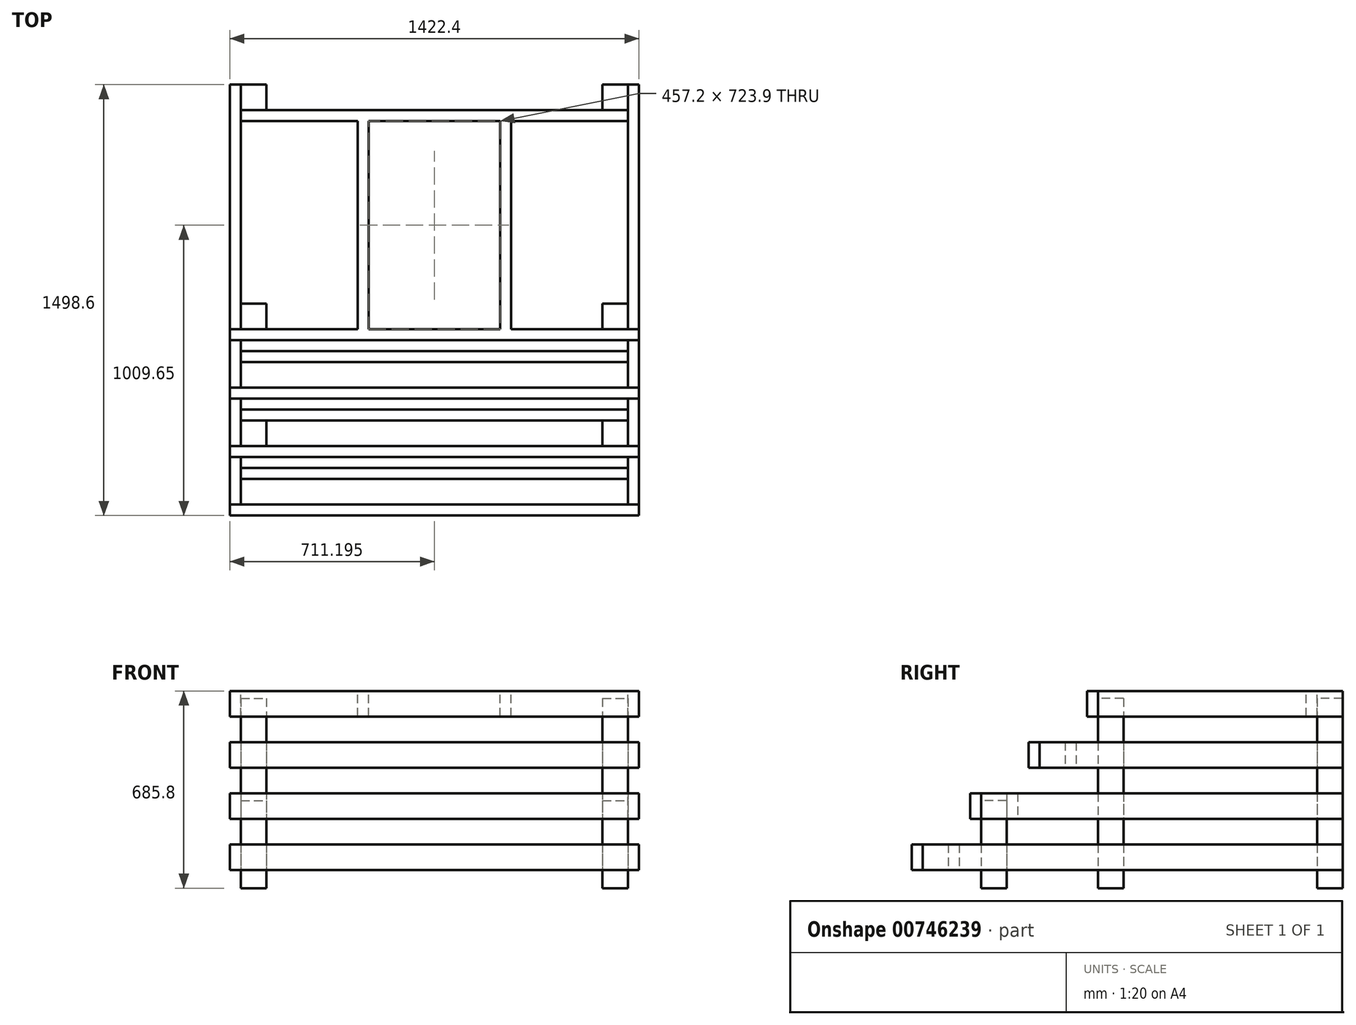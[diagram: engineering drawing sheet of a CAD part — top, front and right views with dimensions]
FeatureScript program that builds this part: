
annotation { "Feature Type Name" : "Feature", "Feature Type Description" : "" }
export const myFeature = defineFeature(function(context is Context, id is Id, definition is map)
    precondition{}
    {
        {
            var Q0;
            Q0=qCreatedBy(makeId("Top.planeOp"),FACE);
            var sketch = newSketch(context, id + "F0", { "sketchPlane" : qUnion([Q0])});
            skLineSegment(sketch, "E0.bottom", {"start": v(-670.31, 449.54) * mm, "end": v(-581.41, 449.54) * mm});
            skLineSegment(sketch, "E0.top", {"start": v(-670.31, 360.64) * mm, "end": v(-581.41, 360.64) * mm});
            skLineSegment(sketch, "E0.left", {"start": v(-670.31, 449.54) * mm, "end": v(-670.31, 360.64) * mm});
            skLineSegment(sketch, "E0.right", {"start": v(-581.41, 449.54) * mm, "end": v(-581.41, 360.64) * mm});
            skLineSegment(sketch, "E1.bottom", {"start": v(586.99, 449.54) * mm, "end": v(675.89, 449.54) * mm});
            skLineSegment(sketch, "E1.top", {"start": v(586.99, 360.64) * mm, "end": v(675.89, 360.64) * mm});
            skLineSegment(sketch, "E1.left", {"start": v(586.99, 449.54) * mm, "end": v(586.99, 360.64) * mm});
            skLineSegment(sketch, "E1.right", {"start": v(675.89, 449.54) * mm, "end": v(675.89, 360.64) * mm});
            skLineSegment(sketch, "E2.bottom", {"start": v(-670.31, -312.46) * mm, "end": v(-581.41, -312.46) * mm});
            skLineSegment(sketch, "E2.top", {"start": v(-670.31, -401.36) * mm, "end": v(-581.41, -401.36) * mm});
            skLineSegment(sketch, "E2.left", {"start": v(-670.31, -312.46) * mm, "end": v(-670.31, -401.36) * mm});
            skLineSegment(sketch, "E2.right", {"start": v(-581.41, -312.46) * mm, "end": v(-581.41, -401.36) * mm});
            skLineSegment(sketch, "E3.bottom", {"start": v(586.99, -312.46) * mm, "end": v(675.89, -312.46) * mm});
            skLineSegment(sketch, "E3.top", {"start": v(586.99, -401.36) * mm, "end": v(675.89, -401.36) * mm});
            skLineSegment(sketch, "E3.left", {"start": v(586.99, -312.46) * mm, "end": v(586.99, -401.36) * mm});
            skLineSegment(sketch, "E3.right", {"start": v(675.89, -312.46) * mm, "end": v(675.89, -401.36) * mm});
            skLineSegment(sketch, "E4.bottom", {"start": v(-670.31, -718.86) * mm, "end": v(-581.41, -718.86) * mm});
            skLineSegment(sketch, "E4.top", {"start": v(-670.31, -807.76) * mm, "end": v(-581.41, -807.76) * mm});
            skLineSegment(sketch, "E4.left", {"start": v(-670.31, -718.86) * mm, "end": v(-670.31, -807.76) * mm});
            skLineSegment(sketch, "E4.right", {"start": v(-581.41, -718.86) * mm, "end": v(-581.41, -807.76) * mm});
            skLineSegment(sketch, "E5.bottom", {"start": v(586.99, -718.86) * mm, "end": v(675.89, -718.86) * mm});
            skLineSegment(sketch, "E5.top", {"start": v(586.99, -807.76) * mm, "end": v(675.89, -807.76) * mm});
            skLineSegment(sketch, "E5.left", {"start": v(586.99, -718.86) * mm, "end": v(586.99, -807.76) * mm});
            skLineSegment(sketch, "E5.right", {"start": v(675.89, -718.86) * mm, "end": v(675.89, -807.76) * mm});
            skSolve(sketch);
        }
        {
            var Q0;
            Q0 = qSketchRegion(id + "F0", true);
            extrude(context, id + "F1", {"entities" : qUnion([Q0]), "depth" : 660.4 * mm, "offsetDistance" : 25.4 * mm});
        }
        {
            var Q0;
            Q0=qCreatedBy(makeId("Right.planeOp"),FACE);
            var sketch = newSketch(context, id + "F2", { "sketchPlane" : qUnion([Q0])});
            skLineSegment(sketch, "E6.bottom", {"start": v(-597.65, 708) * mm, "end": v(-967.88, 708) * mm});
            skLineSegment(sketch, "E6.top", {"start": v(-597.65, 304.8) * mm, "end": v(-967.88, 304.8) * mm});
            skLineSegment(sketch, "E6.left", {"start": v(-597.65, 708) * mm, "end": v(-597.65, 304.8) * mm});
            skLineSegment(sketch, "E6.right", {"start": v(-967.88, 708) * mm, "end": v(-967.88, 304.8) * mm});
            skSolve(sketch);
        }
        {
            var Q0;
            Q0 = qSketchRegion(id + "F2", true);
            extrude(context, id + "F3", {"entities" : qUnion([Q0]), "operationType" : NewBodyOperationType.REMOVE, "oppositeDirection" : true, "depth" : 1183.64 * mm, "offsetDistance" : 25.4 * mm, "hasSecondDirection" : true, "secondDirectionOppositeDirection" : false, "secondDirectionDepth" : 1132.84 * mm});
        }
        {
            var Q0;
            Q0=makeQuery(id+"F1.opExtrude","SWEPT_FACE",FACE,{"disambiguationData":[OSD([sQuery(id+"F0.wireOp",EDGE,"E4.top")])]});
            var sketch = newSketch(context, id + "F4", { "sketchPlane" : qUnion([Q0])});
            skLineSegment(sketch, "E7.bottom", {"start": v(-670.31, 596.9) * mm, "end": v(-708.41, 596.9) * mm});
            skLineSegment(sketch, "E7.top", {"start": v(-670.31, 685.8) * mm, "end": v(-708.41, 685.8) * mm});
            skLineSegment(sketch, "E7.left", {"start": v(-670.31, 596.9) * mm, "end": v(-670.31, 685.8) * mm});
            skLineSegment(sketch, "E7.right", {"start": v(-708.41, 596.9) * mm, "end": v(-708.41, 685.8) * mm});
            skPoint(sketch, "E8.firstSnap0", {"position": v(-689.36, 596.9) * mm});
            skLineSegment(sketch, "E8.bottom", {"start": v(675.89, 596.9) * mm, "end": v(713.99, 596.9) * mm});
            skLineSegment(sketch, "E8.top", {"start": v(675.89, 685.8) * mm, "end": v(713.99, 685.8) * mm});
            skLineSegment(sketch, "E8.left", {"start": v(675.89, 596.9) * mm, "end": v(675.89, 685.8) * mm});
            skLineSegment(sketch, "E8.right", {"start": v(713.99, 596.9) * mm, "end": v(713.99, 685.8) * mm});
            skLineSegment(sketch, "E9.bottom", {"start": v(-670.31, 241.3) * mm, "end": v(-708.41, 241.3) * mm});
            skLineSegment(sketch, "E9.top", {"start": v(-670.31, 330.2) * mm, "end": v(-708.41, 330.2) * mm});
            skLineSegment(sketch, "E9.left", {"start": v(-670.31, 241.3) * mm, "end": v(-670.31, 330.2) * mm});
            skLineSegment(sketch, "E9.right", {"start": v(-708.41, 241.3) * mm, "end": v(-708.41, 330.2) * mm});
            skLineSegment(sketch, "E10.bottom", {"start": v(675.89, 241.3) * mm, "end": v(713.99, 241.3) * mm});
            skLineSegment(sketch, "E10.top", {"start": v(675.89, 330.2) * mm, "end": v(713.99, 330.2) * mm});
            skLineSegment(sketch, "E10.left", {"start": v(675.89, 241.3) * mm, "end": v(675.89, 330.2) * mm});
            skLineSegment(sketch, "E10.right", {"start": v(713.99, 241.3) * mm, "end": v(713.99, 330.2) * mm});
            skLineSegment(sketch, "E11.bottom", {"start": v(-670.31, 63.5) * mm, "end": v(-708.41, 63.5) * mm});
            skLineSegment(sketch, "E11.top", {"start": v(-670.31, 152.4) * mm, "end": v(-708.41, 152.4) * mm});
            skLineSegment(sketch, "E11.left", {"start": v(-670.31, 63.5) * mm, "end": v(-670.31, 152.4) * mm});
            skLineSegment(sketch, "E11.right", {"start": v(-708.41, 63.5) * mm, "end": v(-708.41, 152.4) * mm});
            skLineSegment(sketch, "E12.bottom", {"start": v(675.89, 63.5) * mm, "end": v(713.99, 63.5) * mm});
            skLineSegment(sketch, "E12.top", {"start": v(675.89, 152.4) * mm, "end": v(713.99, 152.4) * mm});
            skLineSegment(sketch, "E12.left", {"start": v(675.89, 63.5) * mm, "end": v(675.89, 152.4) * mm});
            skLineSegment(sketch, "E12.right", {"start": v(713.99, 63.5) * mm, "end": v(713.99, 152.4) * mm});
            skLineSegment(sketch, "E13.bottom", {"start": v(-708.41, 508) * mm, "end": v(-670.31, 508) * mm});
            skLineSegment(sketch, "E13.top", {"start": v(-708.41, 419.1) * mm, "end": v(-670.31, 419.1) * mm});
            skLineSegment(sketch, "E13.left", {"start": v(-708.41, 508) * mm, "end": v(-708.41, 419.1) * mm});
            skLineSegment(sketch, "E13.right", {"start": v(-670.31, 508) * mm, "end": v(-670.31, 419.1) * mm});
            skLineSegment(sketch, "E14.bottom", {"start": v(713.99, 508) * mm, "end": v(675.89, 508) * mm});
            skLineSegment(sketch, "E14.top", {"start": v(713.99, 419.1) * mm, "end": v(675.89, 419.1) * mm});
            skLineSegment(sketch, "E14.left", {"start": v(713.99, 508) * mm, "end": v(713.99, 419.1) * mm});
            skLineSegment(sketch, "E14.right", {"start": v(675.89, 508) * mm, "end": v(675.89, 419.1) * mm});
            skSolve(sketch);
        }
        {
            var Q0;
            Q0 = qSketchRegion(id + "F4", true);
            var Q1;
            Q1=makeQuery(id+"F1.opExtrude","SWEPT_FACE",FACE,{"disambiguationData":[OSD([sQuery(id+"F0.wireOp",EDGE,"E0.bottom")])]});
            extrude(context, id + "F5", {"entities" : qUnion([Q0]), "endBound" : BoundingType.UP_TO_SURFACE, "oppositeDirection" : true, "depth" : 1033.78 * mm, "endBoundEntityFace" : qUnion([Q1]), "offsetDistance" : 25.4 * mm, "hasSecondDirection" : true, "secondDirectionOppositeDirection" : false, "secondDirectionDepth" : 203.2 * mm});
        }
        {
            var Q0;
            Q0=makeQuery(id+"F5.opExtrude","SWEPT_FACE",FACE,{"disambiguationData":[OSD([sQuery(id+"F4.wireOp",EDGE,"E7.right")])]});
            var sketch = newSketch(context, id + "F6", { "sketchPlane" : qUnion([Q0])});
            skLineSegment(sketch, "E15", {"start": v(401.36, 719.63) * mm, "end": v(401.36, 535.63) * mm});
            skLineSegment(sketch, "E16", {"start": v(401.36, 535.63) * mm, "end": v(604.56, 535.63) * mm});
            skLineSegment(sketch, "E17", {"start": v(604.56, 535.63) * mm, "end": v(604.56, 378.3) * mm});
            skLineSegment(sketch, "E18", {"start": v(604.56, 378.3) * mm, "end": v(807.76, 378.3) * mm});
            skLineSegment(sketch, "E19", {"start": v(807.76, 378.3) * mm, "end": v(807.76, 220.96) * mm});
            skLineSegment(sketch, "E20", {"start": v(807.76, 220.96) * mm, "end": v(1041.36, 220.96) * mm});
            skLineSegment(sketch, "E21", {"start": v(1041.36, 220.96) * mm, "end": v(1041.36, 722.3) * mm});
            skLineSegment(sketch, "E22", {"start": v(1041.36, 722.3) * mm, "end": v(401.36, 719.63) * mm});
            skSolve(sketch);
        }
        {
            var Q0;
            Q0 = qSketchRegion(id + "F6", true);
            extrude(context, id + "F7", {"entities" : qUnion([Q0]), "operationType" : NewBodyOperationType.REMOVE, "oppositeDirection" : true, "depth" : 2004.06 * mm, "offsetDistance" : 25.4 * mm});
        }
        {
            var Q0;
            Q0=makeQuery(id+"F5.opExtrude","SWEPT_FACE",FACE,{"disambiguationData":[OSD([sQuery(id+"F4.wireOp",EDGE,"E7.top")])]});
            var sketch = newSketch(context, id + "F8", { "sketchPlane" : qUnion([Q0])});
            skLineSegment(sketch, "E23.bottom", {"start": v(-670.31, 360.64) * mm, "end": v(675.89, 360.64) * mm});
            skLineSegment(sketch, "E23.top", {"start": v(-670.31, 322.54) * mm, "end": v(675.89, 322.54) * mm});
            skLineSegment(sketch, "E23.left", {"start": v(-670.31, 360.64) * mm, "end": v(-670.31, 322.54) * mm});
            skLineSegment(sketch, "E23.right", {"start": v(675.89, 360.64) * mm, "end": v(675.89, 322.54) * mm});
            skLineSegment(sketch, "E24.bottom", {"start": v(-263.91, 322.54) * mm, "end": v(-225.81, 322.54) * mm});
            skLineSegment(sketch, "E24.top", {"start": v(-263.91, -401.36) * mm, "end": v(-225.81, -401.36) * mm});
            skLineSegment(sketch, "E24.left", {"start": v(-225.81, 322.54) * mm, "end": v(-225.81, -401.36) * mm});
            skLineSegment(sketch, "E24.right", {"start": v(-263.91, 322.54) * mm, "end": v(-263.91, -401.36) * mm});
            skLineSegment(sketch, "E25.bottom", {"start": v(231.39, 322.54) * mm, "end": v(269.49, 322.54) * mm});
            skLineSegment(sketch, "E25.top", {"start": v(231.39, -401.36) * mm, "end": v(269.49, -401.36) * mm});
            skLineSegment(sketch, "E25.left", {"start": v(231.39, 322.54) * mm, "end": v(231.39, -401.36) * mm});
            skLineSegment(sketch, "E25.right", {"start": v(269.49, 322.54) * mm, "end": v(269.49, -401.36) * mm});
            skLineSegment(sketch, "E26.bottom", {"start": v(-708.41, -401.36) * mm, "end": v(713.99, -401.36) * mm});
            skLineSegment(sketch, "E26.top", {"start": v(-708.41, -439.46) * mm, "end": v(713.99, -439.46) * mm});
            skLineSegment(sketch, "E26.left", {"start": v(-708.41, -401.36) * mm, "end": v(-708.41, -439.46) * mm});
            skLineSegment(sketch, "E26.right", {"start": v(713.99, -401.36) * mm, "end": v(713.99, -439.46) * mm});
            skSolve(sketch);
        }
        {
            var Q0;
            Q0 = qSketchRegion(id + "F8", true);
            extrude(context, id + "F9", {"entities" : qUnion([Q0]), "oppositeDirection" : true, "depth" : 88.9 * mm, "offsetDistance" : 25.4 * mm});
        }
        {
            var Q0;
            Q0=makeQuery(id+"F5.opExtrude","SWEPT_FACE",FACE,{"disambiguationData":[OSD([sQuery(id+"F4.wireOp",EDGE,"E13.left")])]});
            var sketch = newSketch(context, id + "F10", { "sketchPlane" : qUnion([Q0])});
            skLineSegment(sketch, "E27.bottom", {"start": v(604.56, 508) * mm, "end": v(642.66, 508) * mm});
            skLineSegment(sketch, "E27.top", {"start": v(604.56, 419.1) * mm, "end": v(642.66, 419.1) * mm});
            skLineSegment(sketch, "E27.left", {"start": v(604.56, 508) * mm, "end": v(604.56, 419.1) * mm});
            skLineSegment(sketch, "E27.right", {"start": v(642.66, 508) * mm, "end": v(642.66, 419.1) * mm});
            skLineSegment(sketch, "E28.bottom", {"start": v(807.76, 330.2) * mm, "end": v(845.86, 330.2) * mm});
            skLineSegment(sketch, "E28.top", {"start": v(807.76, 241.3) * mm, "end": v(845.86, 241.3) * mm});
            skLineSegment(sketch, "E28.left", {"start": v(807.76, 330.2) * mm, "end": v(807.76, 241.3) * mm});
            skLineSegment(sketch, "E28.right", {"start": v(845.86, 330.2) * mm, "end": v(845.86, 241.3) * mm});
            skLineSegment(sketch, "E29.bottom", {"start": v(1010.96, 152.4) * mm, "end": v(1049.06, 152.4) * mm});
            skLineSegment(sketch, "E29.top", {"start": v(1010.96, 63.5) * mm, "end": v(1049.06, 63.5) * mm});
            skLineSegment(sketch, "E29.left", {"start": v(1010.96, 152.4) * mm, "end": v(1010.96, 63.5) * mm});
            skLineSegment(sketch, "E29.right", {"start": v(1049.06, 152.4) * mm, "end": v(1049.06, 63.5) * mm});
            skSolve(sketch);
        }
        {
            var Q0;
            Q0 = qSketchRegion(id + "F10", true);
            var Q1;
            Q1=makeQuery(id+"F5.opExtrude","SWEPT_FACE",FACE,{"disambiguationData":[OSD([sQuery(id+"F4.wireOp",EDGE,"E10.right")])]});
            extrude(context, id + "F11", {"entities" : qUnion([Q0]), "endBound" : BoundingType.UP_TO_SURFACE, "oppositeDirection" : true, "depth" : 25.4 * mm, "endBoundEntityFace" : qUnion([Q1]), "offsetDistance" : 25.4 * mm});
        }
        {
            var Q0;
            Q0=makeQuery(id+"F5.opExtrude","SWEPT_FACE",FACE,{"disambiguationData":[OSD([sQuery(id+"F4.wireOp",EDGE,"E14.right")])]});
            var sketch = newSketch(context, id + "F12", { "sketchPlane" : qUnion([Q0])});
            skLineSegment(sketch, "E30.bottom", {"start": v(477.56, 508) * mm, "end": v(515.66, 508) * mm});
            skLineSegment(sketch, "E30.top", {"start": v(477.56, 419.1) * mm, "end": v(515.66, 419.1) * mm});
            skLineSegment(sketch, "E30.left", {"start": v(477.56, 508) * mm, "end": v(477.56, 419.1) * mm});
            skLineSegment(sketch, "E30.right", {"start": v(515.66, 508) * mm, "end": v(515.66, 419.1) * mm});
            skLineSegment(sketch, "E31.bottom", {"start": v(883.96, 152.4) * mm, "end": v(922.06, 152.4) * mm});
            skLineSegment(sketch, "E31.top", {"start": v(883.96, 63.5) * mm, "end": v(922.06, 63.5) * mm});
            skLineSegment(sketch, "E31.left", {"start": v(883.96, 152.4) * mm, "end": v(883.96, 63.5) * mm});
            skLineSegment(sketch, "E31.right", {"start": v(922.06, 152.4) * mm, "end": v(922.06, 63.5) * mm});
            skLineSegment(sketch, "E32.bottom", {"start": v(718.86, 330.2) * mm, "end": v(680.76, 330.2) * mm});
            skLineSegment(sketch, "E32.top", {"start": v(718.86, 241.3) * mm, "end": v(680.76, 241.3) * mm});
            skLineSegment(sketch, "E32.left", {"start": v(718.86, 330.2) * mm, "end": v(718.86, 241.3) * mm});
            skLineSegment(sketch, "E32.right", {"start": v(680.76, 330.2) * mm, "end": v(680.76, 241.3) * mm});
            skSolve(sketch);
        }
        {
            var Q0;
            Q0 = qSketchRegion(id + "F12", true);
            var Q1;
            Q1=makeQuery(id+"F5.opExtrude","SWEPT_FACE",FACE,{"disambiguationData":[OSD([sQuery(id+"F4.wireOp",EDGE,"E13.right")])]});
            extrude(context, id + "F13", {"entities" : qUnion([Q0]), "endBound" : BoundingType.UP_TO_SURFACE, "depth" : 25.4 * mm, "endBoundEntityFace" : qUnion([Q1]), "offsetDistance" : 25.4 * mm});
        }
    });
